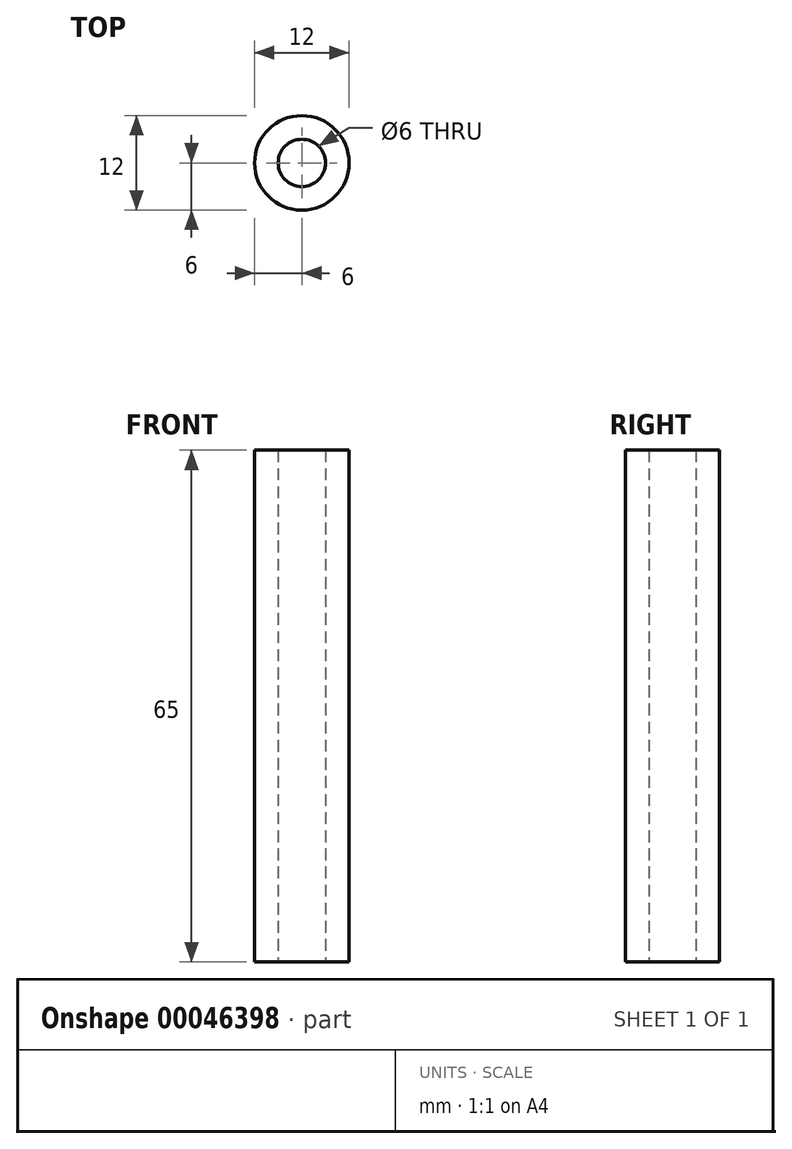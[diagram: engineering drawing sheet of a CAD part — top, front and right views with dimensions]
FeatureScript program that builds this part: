
annotation { "Feature Type Name" : "Feature", "Feature Type Description" : "" }
export const myFeature = defineFeature(function(context is Context, id is Id, definition is map)
    precondition{}
    {
        {
            var Q0;
            Q0=qCreatedBy(makeId("Front.planeOp"),FACE);
            var sketch = newSketch(context, id + "F0", { "sketchPlane" : qUnion([Q0])});
            skLineSegment(sketch, "E0", {"start": v(-6, 0) * mm, "end": v(-6, 65) * mm});
            skLineSegment(sketch, "E1.0", {"start": v(-3, 0) * mm, "end": v(-3, 65) * mm});
            skLineSegment(sketch, "E2", {"start": v(-3, 65) * mm, "end": v(-6, 65) * mm});
            skLineSegment(sketch, "E3", {"start": v(-3, 0) * mm, "end": v(-6, 0) * mm});
            skLineSegment(sketch, "E4", {"start": v(0, 0) * mm, "end": v(0, 68.11) * mm, "construction": true});
            skSolve(sketch);
        }
        {
            var Q0;
            Q0=makeQuery(id+"F0.imprint","IMPRINT",FACE,{"disambiguationData":[TD([[makeQuery(id+"F0.imprint","IMPRINT",EDGE,{"derivedFrom":sQuery(id+"F0.wireOp",EDGE,"E0")}),-1.0]])]});
            var Q1;
            Q1=sQuery(id+"F0.wireOp",EDGE,"E4");
            revolve(context, id + "F1", {"entities" : qUnion([Q0]), "axis" : qUnion([Q1]), "revolveType" : RevolveType.FULL});
        }
    });
